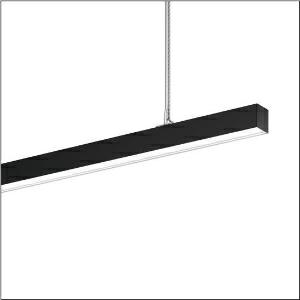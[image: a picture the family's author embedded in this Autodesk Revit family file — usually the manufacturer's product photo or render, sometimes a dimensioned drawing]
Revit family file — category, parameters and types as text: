
# Revit family: silica_r__21_51mx33tctdb_eeca
name_source: partatom
category: Lighting Fixtures
units: mm (PartAtom-declared; Revit-internal decimal feet)

## family parameters
Cut with Voids When Loaded = No
Host = Face
Light Source = No
Part Type = Normal
Room Calculation Point = No
Round Connector Dimension = Use Diameter
Shared = No

## types (1)
- --- (1 x LED, 14340 lm, 134.7 W, 6500K)
    Apparent Load = 135 VA
    CIE Flux Codes = 78 96 99 56 100
    Color Rendering = 80
    Color Temperature = 6500K
    Default Elevation = 1800 mm
    Description = Silica® 21, office luminaire, primary optical cover: prismatic diffuser, of PMMA, CAT 2 (L<= 3000cd/m²), light emission: direct/indirect distribution, primary light characteristic: symmetric, installation type: suspended mounting, LED, rated luminous flux: 14.340lm, luminous efficacy: 101lm/W, light colour: 8tw, colour temperature: 2700..6500K, control gear: ECG DALI, with terminal, 3+2-pole, max. 2.5mm², mains connection: 220..240V, AC, 50/60Hz, rated input power: 141.4W, luminaire housing, of aluminium, jet black (RAL 9005), length: 3.004mm, width: 53mm, height: 53mm, protection rating (complete): IP20, insulation class (complete): insulation class I (protective earthing), certification: CE, permissible operating ambient temperature: 0..+35°C, standard: EN 50419, packaging unit: 1 piece
    Height = 53 mm
    Lamp = 1 x LED
    Lamp Light Flux = 14340 lm
    Lamp Power = 134.7 W
    Lamp count = 1
    Length = 3004 mm
    Luminous efficacy = 106 lm/W
    Manufacturer = Siteco
    ModVariant = No
    Model = 51MX33TCTDB
    Mounting Place = Ceiling
    Mounting Type = Pendant
    Number of Poles = 1
    OnlyDefault = Yes
    Power Factor = 1
    Product Name = Silica® 21
    Product group = office luminaire | ceiling pendant
    ProductGroupID = 902
    Protection Class = Protection class I
    Protection Degree = IP 20
    RLX_Detail_Level = 1
    RLX_Emergency_Light_Flux = 0 lm
    RLX_Emergency_Type = 0
    RLX_Emergency_Type_DB = No
    RlxData = <blob elided: 22849 chars, md5=ed55f0fd>
    Socket = socket
    Standby Power = 0 W
    System Light Flux = 14340 lm
    System Power = 135 W
    Type Comments = individual setting
    Type Image = l_1297744.jpg
    URL = http://relux.com
    VarID = @adj_071077
    Voltage = 0 V
    Weight = 0.00 kg
    Width = 53 mm

## geometry (parser evidence)
native form markers: Blend x4, Sweep x12
no freeform markers — native parametric forms only
